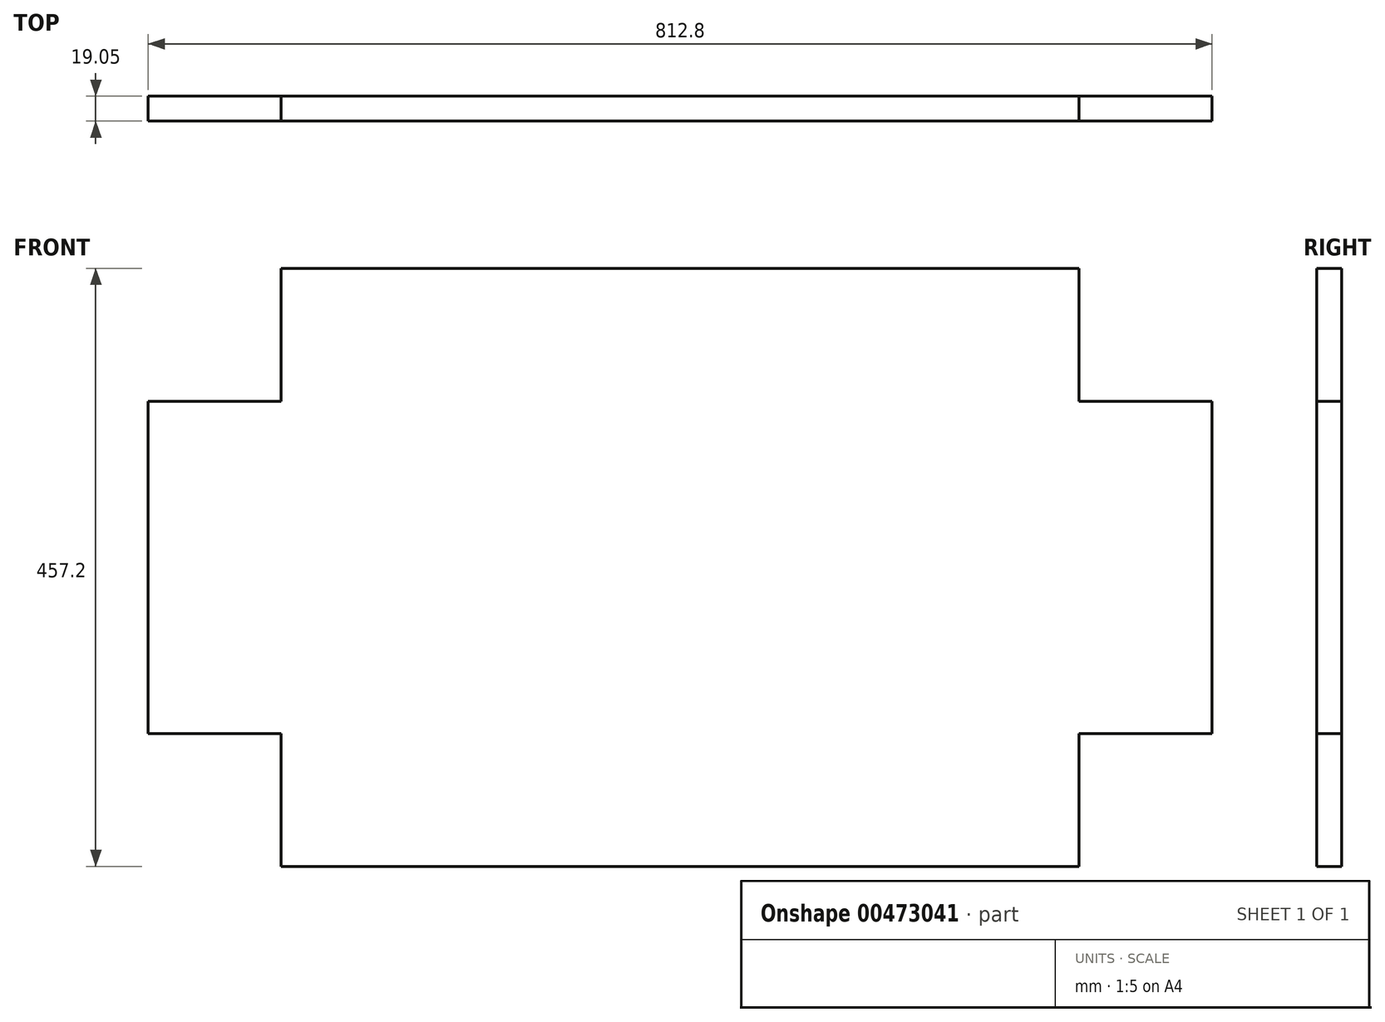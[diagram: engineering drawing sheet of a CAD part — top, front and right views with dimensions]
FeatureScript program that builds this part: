
annotation { "Feature Type Name" : "Feature", "Feature Type Description" : "" }
export const myFeature = defineFeature(function(context is Context, id is Id, definition is map)
    precondition{}
    {
        {
            var Q0;
            Q0=qCreatedBy(makeId("Front.planeOp"),FACE);
            var sketch = newSketch(context, id + "F0", { "sketchPlane" : qUnion([Q0])});
            skLineSegment(sketch, "E0.bottom", {"start": v(304.8, 228.6) * mm, "end": v(-304.8, 228.6) * mm});
            skLineSegment(sketch, "E0.top", {"start": v(304.8, -228.6) * mm, "end": v(-304.8, -228.6) * mm});
            skLineSegment(sketch, "E0.left", {"start": v(406.4, 127) * mm, "end": v(406.4, -127) * mm});
            skLineSegment(sketch, "E0.right", {"start": v(-406.4, 127) * mm, "end": v(-406.4, -127) * mm});
            skPoint(sketch, "E0.middle", {"position": v(0, 0) * mm});
            skLineSegment(sketch, "E1.0", {"start": v(406.4, -127) * mm, "end": v(304.8, -127) * mm});
            skLineSegment(sketch, "E2.0", {"start": v(-304.8, 228.6) * mm, "end": v(-304.8, 127) * mm});
            skLineSegment(sketch, "E3.0", {"start": v(406.4, 127) * mm, "end": v(304.8, 127) * mm});
            skLineSegment(sketch, "E4.0", {"start": v(304.8, 228.6) * mm, "end": v(304.8, 127) * mm});
            skPoint(sketch, "E5.orphan", {"position": v(-406.4, 228.6) * mm});
            skPoint(sketch, "E6.orphan", {"position": v(406.4, 228.6) * mm});
            skPoint(sketch, "E7.orphan", {"position": v(406.4, -228.6) * mm});
            skPoint(sketch, "E8.orphan", {"position": v(-406.4, -228.6) * mm});
            skLineSegment(sketch, "E9.trimOffspring", {"start": v(-304.8, -127) * mm, "end": v(-304.8, -228.6) * mm});
            skLineSegment(sketch, "E10.trimOffspring", {"start": v(-304.8, 127) * mm, "end": v(-406.4, 127) * mm});
            skLineSegment(sketch, "E11.trimOffspring", {"start": v(304.8, -127) * mm, "end": v(304.8, -228.6) * mm});
            skLineSegment(sketch, "E12.trimOffspring", {"start": v(-304.8, -127) * mm, "end": v(-406.4, -127) * mm});
            skSolve(sketch);
        }
        {
            var Q0;
            Q0=makeQuery(id+"F0.imprint","IMPRINT",FACE,{"disambiguationData":[TD([[makeQuery(id+"F0.imprint","IMPRINT",EDGE,{"derivedFrom":sQuery(id+"F0.wireOp",EDGE,"E0.bottom")}),1.0]])]});
            extrude(context, id + "F1", {"entities" : qUnion([Q0]), "depth" : 19.05 * mm});
        }
    });
